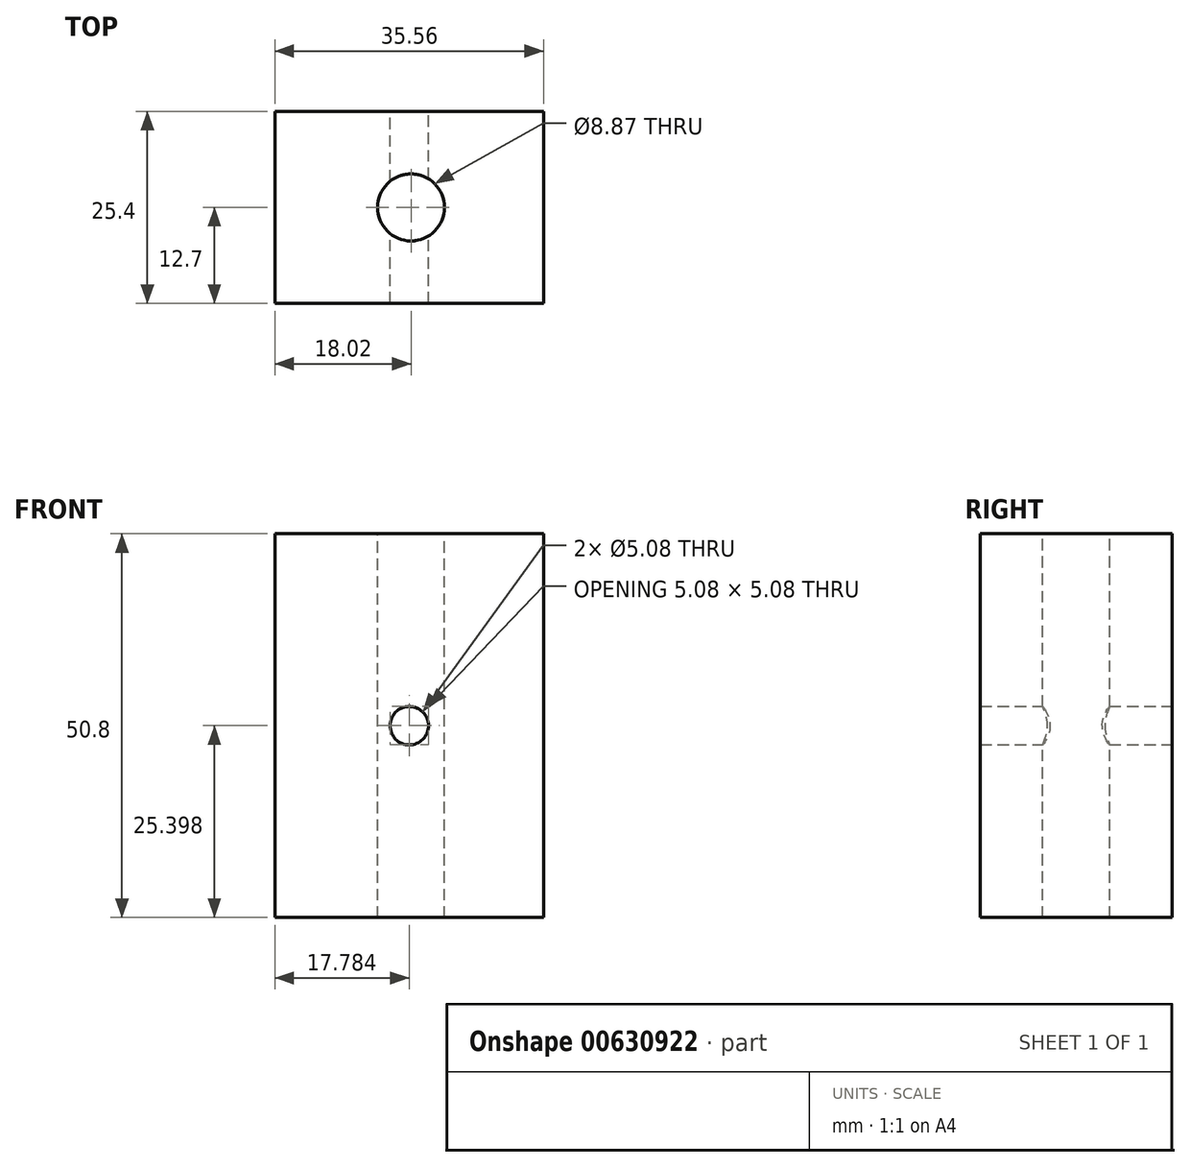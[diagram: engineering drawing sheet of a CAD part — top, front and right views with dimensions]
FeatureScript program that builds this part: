
annotation { "Feature Type Name" : "Feature", "Feature Type Description" : "" }
export const myFeature = defineFeature(function(context is Context, id is Id, definition is map)
    precondition{}
    {
        {
            var Q0;
            Q0=qCreatedBy(makeId("Front.planeOp"),FACE);
            var sketch = newSketch(context, id + "F0", { "sketchPlane" : qUnion([Q0])});
            skLineSegment(sketch, "E0.bottom", {"start": v(17.54, -56.1) * mm, "end": v(-18.02, -56.1) * mm});
            skLineSegment(sketch, "E0.top", {"start": v(17.54, -5.3) * mm, "end": v(-18.02, -5.3) * mm});
            skLineSegment(sketch, "E0.left", {"start": v(17.54, -56.1) * mm, "end": v(17.54, -5.3) * mm});
            skLineSegment(sketch, "E0.right", {"start": v(-18.02, -56.1) * mm, "end": v(-18.02, -5.3) * mm});
            skCircle(sketch, "E1", {"center": v(-0.24, -30.7) * mm, "radius": 2.54 * mm});
            skSolve(sketch);
        }
        {
            var Q0;
            Q0 = qSketchRegion(id + "F0", true);
            extrude(context, id + "F1", {"entities" : qUnion([Q0]), "depth" : 25.4 * mm, "offsetDistance" : 25.4 * mm});
        }
        {
            var Q0;
            Q0=makeQuery(id+"F1.opExtrude","SWEPT_FACE",FACE,{"disambiguationData":[OSD([sQuery(id+"F0.wireOp",EDGE,"E0.top")])]});
            var sketch = newSketch(context, id + "F2", { "sketchPlane" : qUnion([Q0])});
            skCircle(sketch, "E2", {"center": v(0, -12.7) * mm, "radius": 4.43 * mm});
            skSolve(sketch);
        }
        {
            var Q0;
            Q0 = qSketchRegion(id + "F2", true);
            extrude(context, id + "F3", {"entities" : qUnion([Q0]), "operationType" : NewBodyOperationType.REMOVE, "oppositeDirection" : true, "depth" : 127 * mm, "offsetDistance" : 25.4 * mm});
        }
    });
